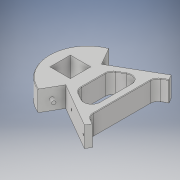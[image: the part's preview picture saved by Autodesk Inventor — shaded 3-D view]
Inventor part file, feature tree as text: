
AUTODESK INVENTOR PART (.ipt)
format: ipt  version: 2019 (Build 230136000, 136)  size: 243,712 bytes
history: native  units: mm
features: sketch x6, fillet x5, extrude x4, hole x2
ambient origin geometry x8: Origin, YZ Plane, XZ Plane, XY Plane, X Axis, Y Axis, Z Axis, Center Point
bodies: Solid1 (feature_tree)
feature tree (17):
  extrude  "Extrusion1"  Depth=100.0mm
  extrude  "Extrusion2"  Depth=20.0mm
  extrude  "Extrusion3"  Depth=6.8mm
  extrude  "Extrusion4"  Depth=10.0mm
  fillet  "Fillet1"  Radius=10.0mm
  fillet  "Fillet2"  Radius=40.0mm
  fillet  "Fillet3"  Radius=40.0mm
  hole  "Hole1"  [1 undecoded]
  hole  "Hole2"  [1 undecoded]
  fillet  "Fillet8"  Radius=25.0mm
  fillet  "Fillet9"  Radius=40.0mm
  sketch  "Sketch1"  dims[d3=40.0mm d4=100.0mm]
  sketch  "Sketch2"  dims[d5=12.0mm d7=20.0mm]
  sketch  "Sketch3"  dims[d8=40.0mm d9=0.0mm d10=6.8mm]
  sketch  "Sketch4"  dims[d11=10.0mm d12=0.0mm d13=6.8mm d14=10.0mm d15=0.0mm d16=40.0mm d17=40.0mm]
  sketch  "Sketch5"  dims[d19=70.0mm d20=75.0mm]
  sketch  "Sketch6"  dims[d21=15.0mm d22=50.0mm d23=25.0mm d24=40.0mm d25=0.0mm d26=15.0mm d27=15.0mm d28=15.0mm d29=4.0mm d30=6.0mm d31=5.0mm d32=2.0mm d33=14.3117mm d34=4.0mm d35=0.0mm d36=4.0mm d37=6.0mm d38=5.0mm d39=2.0mm d40=14.3117mm d41=4.0mm d42=0.0mm d47=1.0mm d48=1.0mm]
note: 2 required parameter values undecoded (feature->parameter linkage not recoverable at this tier; creation-order binding heuristic only, values carry confidence <= 0.55)
